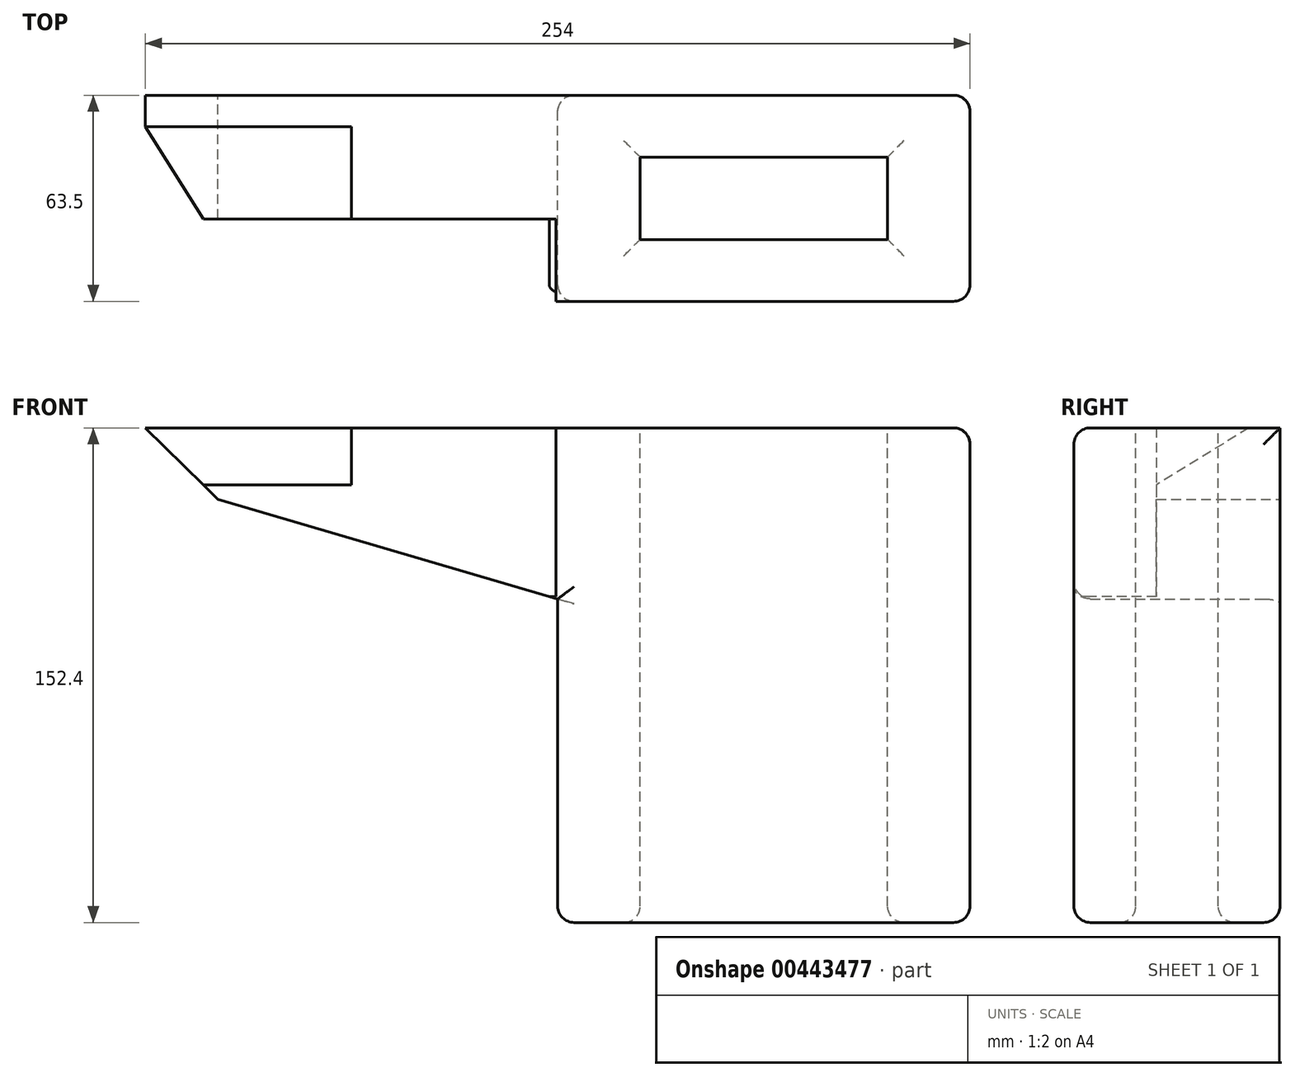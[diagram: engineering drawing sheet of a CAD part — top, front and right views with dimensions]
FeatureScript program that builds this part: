
annotation { "Feature Type Name" : "Feature", "Feature Type Description" : "" }
export const myFeature = defineFeature(function(context is Context, id is Id, definition is map)
    precondition{}
    {
        {
            var Q0;
            Q0=qCreatedBy(makeId("Front.planeOp"),FACE);
            var sketch = newSketch(context, id + "F0", { "sketchPlane" : qUnion([Q0])});
            skLineSegment(sketch, "E0", {"start": v(0, 0) * mm, "end": v(254, 0) * mm});
            skLineSegment(sketch, "E1", {"start": v(0, 0) * mm, "end": v(22.32, -21.97) * mm});
            skLineSegment(sketch, "E2", {"start": v(254, 0) * mm, "end": v(254, -152.4) * mm});
            skLineSegment(sketch, "E3", {"start": v(254, -152.4) * mm, "end": v(127, -152.4) * mm});
            skLineSegment(sketch, "E4", {"start": v(127, -152.4) * mm, "end": v(127, -52.7) * mm});
            skLineSegment(sketch, "E5", {"start": v(127, -52.7) * mm, "end": v(22.32, -21.97) * mm});
            skSolve(sketch);
        }
        {
            var Q0;
            Q0=makeQuery(id+"F0.imprint","IMPRINT",FACE,{"disambiguationData":[TD([[makeQuery(id+"F0.imprint","IMPRINT",EDGE,{"derivedFrom":sQuery(id+"F0.wireOp",EDGE,"E0")}),-1.0]])]});
            extrude(context, id + "F1", {"entities" : qUnion([Q0]), "depth" : 63.5 * mm});
        }
        {
            var Q0;
            Q0=makeQuery(id+"F1.opExtrude","SWEPT_FACE",FACE,{"disambiguationData":[OSD([sQuery(id+"F0.wireOp",EDGE,"E0")])]});
            var sketch = newSketch(context, id + "F2", { "sketchPlane" : qUnion([Q0])});
            skLineSegment(sketch, "E6", {"start": v(254, -31.75) * mm, "end": v(228.6, -31.75) * mm});
            skLineSegment(sketch, "E7", {"start": v(228.6, -31.75) * mm, "end": v(152.4, -31.75) * mm});
            skLineSegment(sketch, "E8", {"start": v(152.4, -31.75) * mm, "end": v(127, -31.75) * mm});
            skLineSegment(sketch, "E9", {"start": v(152.4, -31.75) * mm, "end": v(152.4, -19.05) * mm});
            skLineSegment(sketch, "E10", {"start": v(152.4, -19.05) * mm, "end": v(228.6, -19.05) * mm});
            skLineSegment(sketch, "E11", {"start": v(228.6, -19.05) * mm, "end": v(228.6, -31.75) * mm});
            skLineSegment(sketch, "E12", {"start": v(228.6, -31.75) * mm, "end": v(228.6, -44.45) * mm});
            skLineSegment(sketch, "E13", {"start": v(228.6, -44.45) * mm, "end": v(152.4, -44.45) * mm});
            skLineSegment(sketch, "E14", {"start": v(152.4, -44.45) * mm, "end": v(152.4, -31.75) * mm});
            skSolve(sketch);
        }
        {
            var Q0;
            Q0=makeQuery(id+"F2.imprint","IMPRINT",FACE,{"disambiguationData":[TD([[makeQuery(id+"F2.imprint","IMPRINT",EDGE,{"derivedFrom":sQuery(id+"F2.wireOp",EDGE,"E7")}),-1.0]])]});
            var Q1;
            Q1=makeQuery(id+"F2.imprint","IMPRINT",FACE,{"disambiguationData":[TD([[makeQuery(id+"F2.imprint","IMPRINT",EDGE,{"derivedFrom":sQuery(id+"F2.wireOp",EDGE,"E7")}),1.0]])]});
            extrude(context, id + "F3", {"entities" : qUnion([Q0, Q1]), "operationType" : NewBodyOperationType.REMOVE, "oppositeDirection" : true, "depth" : 304.8 * mm});
        }
        {
            var Q0;
            Q0=makeQuery(id+"F1.opExtrude","CAP_FACE",FACE,{"disambiguationData":[OSD([sQuery(id+"F0.wireOp",EDGE,"E0"),sQuery(id+"F0.wireOp",EDGE,"E1"),sQuery(id+"F0.wireOp",EDGE,"E2"),sQuery(id+"F0.wireOp",EDGE,"E3"),sQuery(id+"F0.wireOp",EDGE,"E4"),sQuery(id+"F0.wireOp",EDGE,"E5")])],"isStart":false});
            var sketch = newSketch(context, id + "F4", { "sketchPlane" : qUnion([Q0])});
            skLineSegment(sketch, "E15", {"start": v(0, 0) * mm, "end": v(63.5, 0) * mm});
            skSolve(sketch);
        }
        {
            var Q0;
            Q0=qCreatedBy(makeId("Right.planeOp"),FACE);
            var sketch = newSketch(context, id + "F5", { "sketchPlane" : qUnion([Q0])});
            skLineSegment(sketch, "E16", {"start": v(0, 0) * mm, "end": v(-63.57, 0) * mm});
            skLineSegment(sketch, "E17", {"start": v(-63.57, 0) * mm, "end": v(-63.57, -13.34) * mm});
            skLineSegment(sketch, "E18", {"start": v(-63.57, -13.34) * mm, "end": v(-48.47, 0) * mm});
            skSolve(sketch);
        }
        {
            var Q0;
            {var subQ0=sQuery(id+"F5.wireOp",EDGE,"E17");Q0=makeQuery(id+"F5.imprint","IMPRINT",FACE,{"disambiguationData":[TD([[makeQuery(id+"F5.imprint","IMPRINT",EDGE,{"derivedFrom":subQ0}),1.0]])]});}
            extrude(context, id + "F6", {"entities" : qUnion([Q0]), "operationType" : NewBodyOperationType.REMOVE, "depth" : 63.5 * mm});
        }
        {
            var Q0;
            Q0=makeQuery(id+"F1.opExtrude","SWEPT_EDGE",EDGE,{"disambiguationData":[OSD([sQuery(id+"F0.wireOp",EDGE,"E0"),sQuery(id+"F0.wireOp",EDGE,"E2")])]});
            var Q1;
            Q1=makeQuery(id+"F1.opExtrude","SWEPT_FACE",FACE,{"disambiguationData":[OSD([sQuery(id+"F0.wireOp",EDGE,"E3")])]});
            var Q2;
            Q2=makeQuery(id+"F1.opExtrude","SWEPT_FACE",FACE,{"disambiguationData":[OSD([sQuery(id+"F0.wireOp",EDGE,"E2")])]});
            var Q3;
            Q3=makeQuery(id+"F1.opExtrude","CAP_EDGE",EDGE,{"disambiguationData":[OSD([sQuery(id+"F0.wireOp",EDGE,"E4")])],"isStart":false});
            var Q4;
            Q4=makeQuery(id+"F1.opExtrude","CAP_EDGE",EDGE,{"disambiguationData":[OSD([sQuery(id+"F0.wireOp",EDGE,"E4")])],"isStart":true});
            fillet(context, id + "F7", {"entities" : qUnion([Q0, Q1, Q2, Q3, Q4]), "radius" : 5.08 * mm, "tangentPropagation" : true, "allowEdgeOverflow" : false});
        }
        {
            var Q0;
            {var subQ2=sQuery(id+"F4.wireOp",EDGE,"E15");Q0=makeQuery(id+"F4.imprint","IMPRINT",FACE,{"disambiguationData":[TD([[makeQuery(id+"F4.imprint","IMPRINT",EDGE,{"derivedFrom":subQ2}),-1.0]])]});}
            var sketch = newSketch(context, id + "F8", { "sketchPlane" : qUnion([Q0])});
            skLineSegment(sketch, "E19", {"start": v(126.46, 0) * mm, "end": v(126.46, -51.95) * mm});
            skLineSegment(sketch, "E20", {"start": v(126.46, -51.95) * mm, "end": v(0, -51.95) * mm});
            skLineSegment(sketch, "E21", {"start": v(0, -51.95) * mm, "end": v(0, 0) * mm});
            skSolve(sketch);
        }
        {
            var Q0;
            {var subQ3=sQuery(id+"F8.wireOp",EDGE,"E19");Q0=makeQuery(id+"F8.imprint","IMPRINT",FACE,{"disambiguationData":[TD([[makeQuery(id+"F8.imprint","IMPRINT",EDGE,{"derivedFrom":subQ3}),-1.0]])]});}
            extrude(context, id + "F9", {"entities" : qUnion([Q0]), "operationType" : NewBodyOperationType.REMOVE, "oppositeDirection" : true, "depth" : 25.4 * mm});
        }
        {
            var Q0;
            Q0=makeQuery(id+"F9.boolean.opBoolean","COPY",EDGE,{"derivedFrom":makeQuery(id+"F9.opExtrude","CAP_EDGE",EDGE,{"disambiguationData":[OSD([sQuery(id+"F8.wireOp",EDGE,"E19")])],"isStart":true})});
            var Q1;
            Q1=makeQuery(id+"F1.opExtrude","CAP_EDGE",EDGE,{"disambiguationData":[OSD([sQuery(id+"F0.wireOp",EDGE,"E0")])],"isStart":false});
            var Q2;
            Q2=makeQuery(id+"F1.opExtrude","CAP_EDGE",EDGE,{"disambiguationData":[OSD([sQuery(id+"F0.wireOp",EDGE,"E5")])],"isStart":false});
            fillet(context, id + "F10", {"entities" : qUnion([Q0, Q1, Q2]), "radius" : 5.08 * mm, "tangentPropagation" : true, "allowEdgeOverflow" : false});
        }
        {
            var Q0;
            Q0=qCreatedBy(makeId("Right.planeOp"),FACE);
            var sketch = newSketch(context, id + "F11", { "sketchPlane" : qUnion([Q0])});
            skLineSegment(sketch, "E22", {"start": v(0, 0) * mm, "end": v(-38.1, 0) * mm});
            skLineSegment(sketch, "E23", {"start": v(-38.1, 0) * mm, "end": v(-38.1, -17.54) * mm});
            skLineSegment(sketch, "E24", {"start": v(-38.1, -17.54) * mm, "end": v(-9.65, 0) * mm});
            skSolve(sketch);
        }
        {
            var Q0;
            Q0 = qSketchRegion(id + "F11", true);
            extrude(context, id + "F12", {"entities" : qUnion([Q0]), "operationType" : NewBodyOperationType.REMOVE, "depth" : 63.5 * mm});
        }
    });
